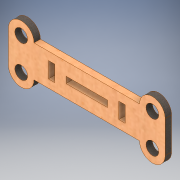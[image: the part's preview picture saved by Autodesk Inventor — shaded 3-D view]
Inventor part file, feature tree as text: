
AUTODESK INVENTOR PART (.ipt)
format: ipt  version: 2019 (Build 230136000, 136)  size: 161,792 bytes
history: native  units: mm
features: other x1, extrude x1, sketch x1
ambient origin geometry x8: Origin, YZ Plane, XZ Plane, XY Plane, X Axis, Y Axis, Z Axis, Center Point
bodies: Body1 (feature_tree)
feature tree (3):
  other  "Твердое тело1"
  extrude  "Выдавливание1"  Depth=8.0mm
  sketch  "Эскиз1"
